# Revit family: ASSA_ABLOY_DockLeveler_DL6210SA
name_source: partatom
category: Mechanical Equipment
units: mm (PartAtom-declared; Revit-internal decimal feet)

## family parameters
Always vertical = Yes
Classification = None
Cut with Voids When Loaded = No
Part Type = Normal
Room Calculation Point = No
Round Connector Dimension = Use Diameter
Shared = No
Work Plane-Based = No

## types (4) — shared parameters
DL6210SBentLip = DL6210S_Platform : DL6210S_BentLip
DL6210SStraightLip = DL6210S_Platform : DL6210S_StraightLip
Description = Dock Leveler
Manufacturer = ASSA ABLOY
Model = DL6210SA
VoidCircle = 1300 mm  [stored 4.26509 ft]

## per-type parameters (varying)
| type | LipType |
| DL6210SA_StraightLip | DL6210S_Platform : DL6210S_StraightLip |
| DL6210SA_BentLip | DL6210S_Platform : DL6210S_BentLip |
| DL6010SA_StraightLip | DL6210S_Platform : DL6210S_StraightLip |
| DL6010SA_BentLip | DL6210S_Platform : DL6210S_StraightLip |

note: [stored X ft] marks values corroborated as IEEE doubles in the binary element streams (Revit-internal decimal feet)

## geometry (parser evidence)
native form markers: Sweep x13
no freeform markers — native parametric forms only
